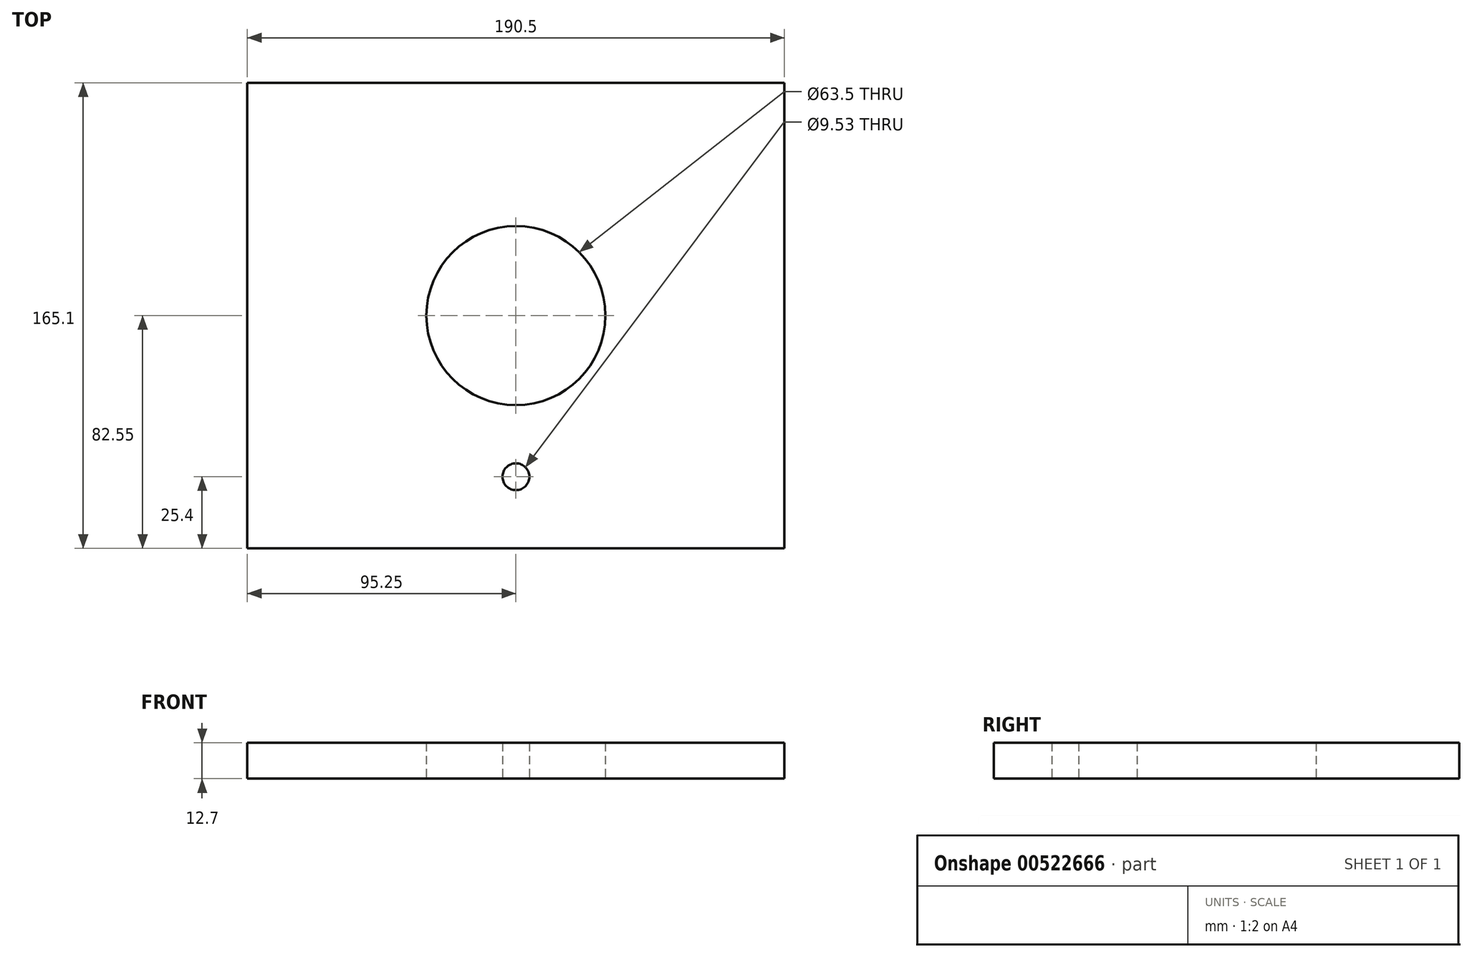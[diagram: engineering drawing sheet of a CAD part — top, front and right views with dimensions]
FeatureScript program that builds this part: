
annotation { "Feature Type Name" : "Feature", "Feature Type Description" : "" }
export const myFeature = defineFeature(function(context is Context, id is Id, definition is map)
    precondition{}
    {
        {
            var Q0;
            Q0=qCreatedBy(makeId("Top.planeOp"),FACE);
            var sketch = newSketch(context, id + "F0", { "sketchPlane" : qUnion([Q0])});
            skLineSegment(sketch, "E0.bottom", {"start": v(95.25, 82.55) * mm, "end": v(-95.25, 82.55) * mm});
            skLineSegment(sketch, "E0.top", {"start": v(95.25, -82.55) * mm, "end": v(-95.25, -82.55) * mm});
            skLineSegment(sketch, "E0.left", {"start": v(95.25, 82.55) * mm, "end": v(95.25, -82.55) * mm});
            skLineSegment(sketch, "E0.right", {"start": v(-95.25, 82.55) * mm, "end": v(-95.25, -82.55) * mm});
            skPoint(sketch, "E1", {"position": v(-95.25, 0) * mm});
            skCircle(sketch, "E2", {"center": v(0, 0) * mm, "radius": 6.35 * mm});
            skPoint(sketch, "E3", {"position": v(6.35, 0) * mm});
            skPoint(sketch, "E4", {"position": v(-6.35, 0) * mm});
            skPoint(sketch, "E5", {"position": v(0, -6.35) * mm});
            skCircle(sketch, "E6", {"center": v(0, 0) * mm, "radius": 31.75 * mm});
            skCircle(sketch, "E7", {"center": v(0, -57.15) * mm, "radius": 4.76 * mm});
            skPoint(sketch, "E8", {"position": v(0, 31.75) * mm});
            skSolve(sketch);
        }
        {
            var Q0;
            Q0=makeQuery(id+"F0.imprint","IMPRINT",FACE,{"disambiguationData":[TD([[makeQuery(id+"F0.imprint","IMPRINT",EDGE,{"derivedFrom":sQuery(id+"F0.wireOp",EDGE,"E0.bottom")}),1.0]])]});
            extrude(context, id + "F1", {"entities" : qUnion([Q0]), "depth" : 12.7 * mm, "offsetDistance" : 25.4 * mm});
        }
    });
